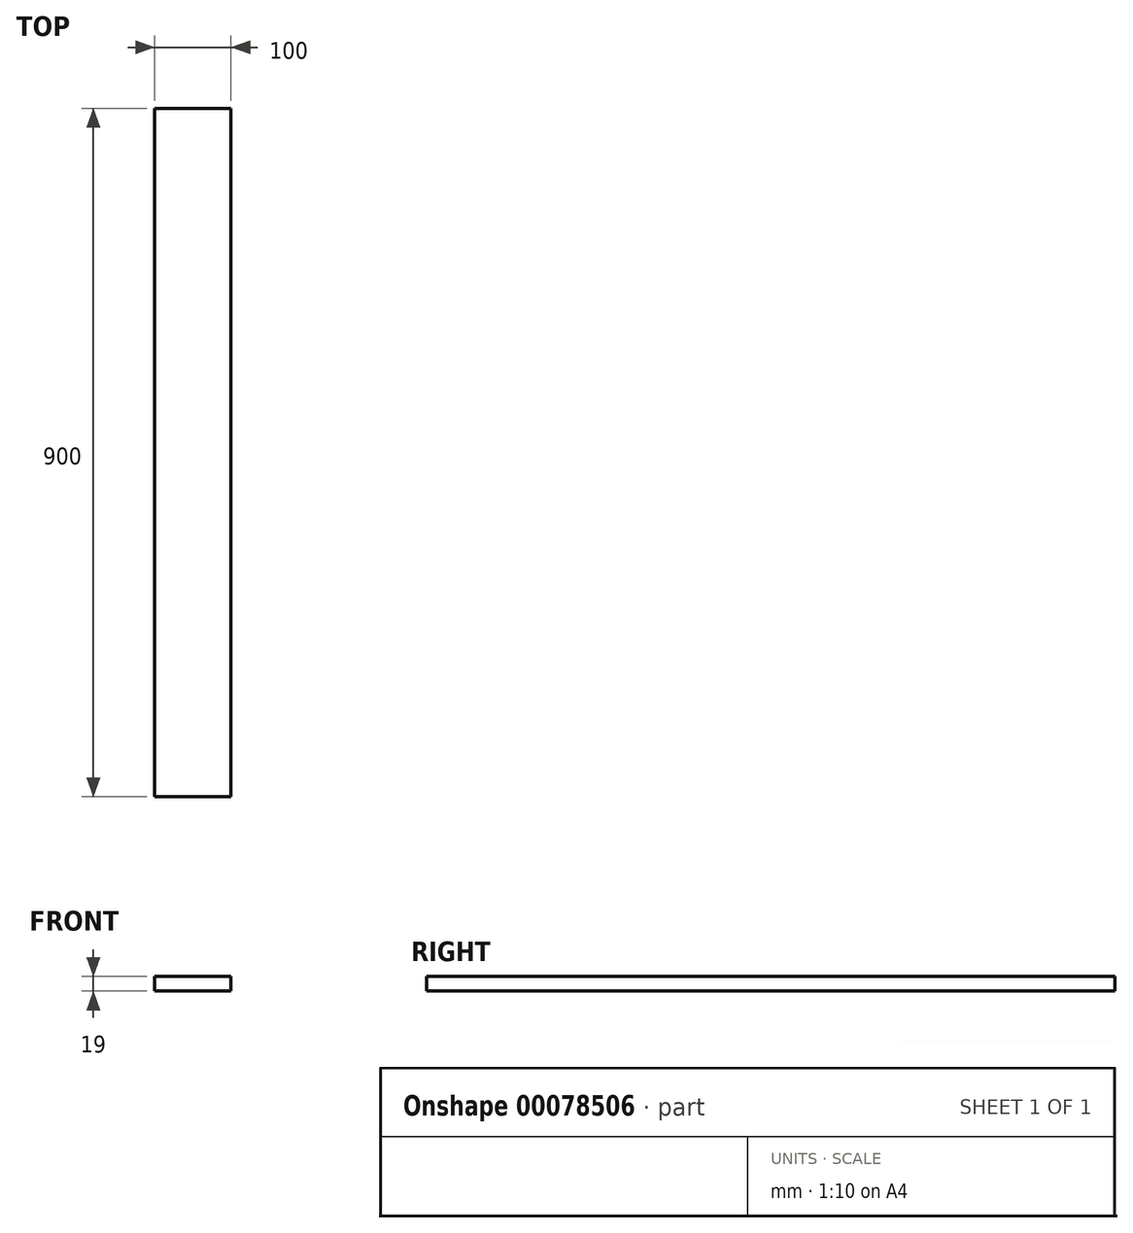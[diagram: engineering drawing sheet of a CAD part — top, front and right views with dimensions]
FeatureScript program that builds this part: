
annotation { "Feature Type Name" : "Feature", "Feature Type Description" : "" }
export const myFeature = defineFeature(function(context is Context, id is Id, definition is map)
    precondition{}
    {
        {
            var Q0;
            Q0=qCreatedBy(makeId("Front.planeOp"),FACE);
            var sketch = newSketch(context, id + "F0", { "sketchPlane" : qUnion([Q0])});
            skLineSegment(sketch, "E0.bottom", {"start": v(50, -9.5) * mm, "end": v(-50, -9.5) * mm});
            skLineSegment(sketch, "E0.top", {"start": v(50, 9.5) * mm, "end": v(-50, 9.5) * mm});
            skLineSegment(sketch, "E0.left", {"start": v(50, -9.5) * mm, "end": v(50, 9.5) * mm});
            skLineSegment(sketch, "E0.right", {"start": v(-50, -9.5) * mm, "end": v(-50, 9.5) * mm});
            skPoint(sketch, "E0.middle", {"position": v(0, 0) * mm});
            skSolve(sketch);
        }
        {
            var Q0;
            Q0=makeQuery(id+"F0.imprint","IMPRINT",FACE,{"disambiguationData":[TD([[makeQuery(id+"F0.imprint","IMPRINT",EDGE,{"derivedFrom":sQuery(id+"F0.wireOp",EDGE,"E0.bottom")}),-1.0]])]});
            extrude(context, id + "F1", {"entities" : qUnion([Q0]), "endBound" : BoundingType.SYMMETRIC, "depth" : 900 * mm});
        }
    });
